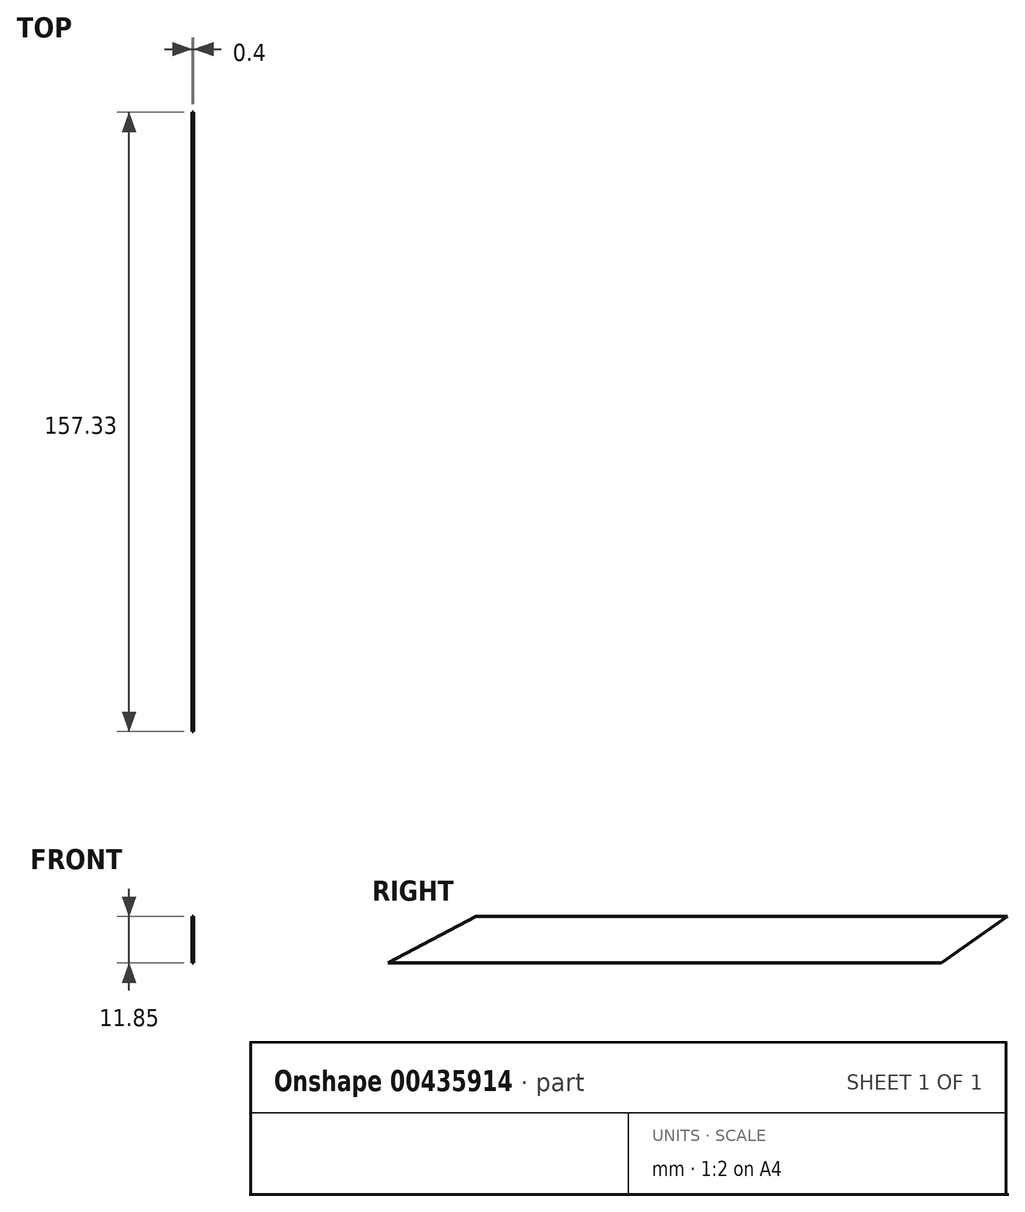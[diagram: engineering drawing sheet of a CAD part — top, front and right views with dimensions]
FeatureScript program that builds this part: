
annotation { "Feature Type Name" : "Feature", "Feature Type Description" : "" }
export const myFeature = defineFeature(function(context is Context, id is Id, definition is map)
    precondition{}
    {
        {
            var Q0;
            Q0=qCreatedBy(makeId("Right.planeOp"),FACE);
            var sketch = newSketch(context, id + "F0", { "sketchPlane" : qUnion([Q0])});
            skLineSegment(sketch, "E0", {"start": v(-63.98, 0) * mm, "end": v(-41.62, 11.85) * mm});
            skLineSegment(sketch, "E1", {"start": v(-41.62, 11.85) * mm, "end": v(93.35, 11.85) * mm});
            skLineSegment(sketch, "E2", {"start": v(93.35, 11.85) * mm, "end": v(76.64, 0) * mm});
            skLineSegment(sketch, "E3", {"start": v(76.64, 0) * mm, "end": v(-63.98, 0) * mm});
            skSolve(sketch);
        }
        {
            var Q0;
            Q0=makeQuery(id+"F0.imprint","IMPRINT",FACE,{"disambiguationData":[TD([[makeQuery(id+"F0.imprint","IMPRINT",EDGE,{"derivedFrom":sQuery(id+"F0.wireOp",EDGE,"E0")}),-1.0]])]});
            extrude(context, id + "F1", {"entities" : qUnion([Q0]), "endBound" : BoundingType.SYMMETRIC, "depth" : 0.4 * mm});
        }
    });
